# Revit family: Accessory-Cabinet_Knob-KOHLER-ARTIFACTS-K-72578T_1
name_source: partatom
category: Specialty Equipment
units: mm (PartAtom-declared; Revit-internal decimal feet)

## family parameters
Cut with Voids When Loaded = No
Host = Face
OmniClass Number = 23.21.19.17.13
OmniClass Title = Casework Component Hardware
Part Type = Normal
Room Calculation Point = No
Round Connector Dimension = Use Diameter
Shared = No

## types (6) — shared parameters
ADA Compliant = No
Assembly Code = C1030200
Date Modified = 08/10/2022
Default Elevation = 42"
Description = Cabinet Knob
Height = 1"
Length = 1"
Manufacturer = Kohler Co.
Master Format 2014 = 10 28 00
Master Format 2014 Name = Toilet, Bath, and Laundry Accessories
Material = Premium Metal Construction
Product Name = ARTIFACTS
URL = http://www.kohler.com.cn
WaterSense Certified = No
Width = 1 3/16"

## per-type parameters (varying)
| type | Finish | Model | Type |
| CP-Polished Chrome | Kohler-Metal-CP-Polished_Chrome | K-72578T-CP | 1 |
| BV-Brushed Bronze | Kohler-Metal-BV-Brushed_Bronze | K-72578T-BV | 2 |
| BN-Vibrant Brushed Nickel | Kohler-Metal-BN-Vibrant_Brushed_Nickel | K-72578T-BN | 3 |
| AF-Vibrant French Gold | Kohler-Metal-AF-Vibrant_French_Gold | K-72578T-AF | 4 |
| 2BZ-Oil Rubbed Bronze | Kohler-Metal-2BZ-Oil_Rubbed_Bronze | K-72578T-2BZ | 5 |
| RGD-Polished Rose Gold | Kohler-Metal-RGD-Polished_Rose_Gold | K-72578T-RGD | 6 |

## geometry (parser evidence)
native form markers: Sweep x4
no freeform markers — native parametric forms only
